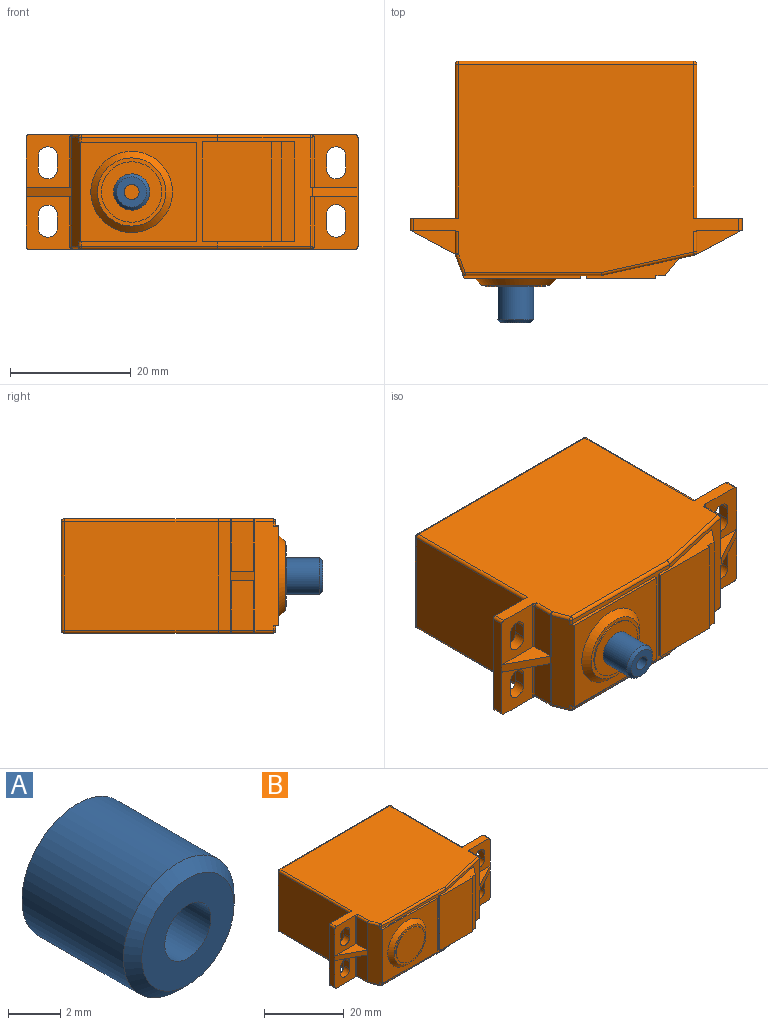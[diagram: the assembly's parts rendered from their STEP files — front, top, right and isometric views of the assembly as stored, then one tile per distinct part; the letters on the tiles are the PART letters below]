
ASSEMBLY  parts=2 mates=1
PART A: 5 faces, bbox 6x6x6 mm
  f0: cylinder r=3mm len=6mm, axis (0,1,0), area 103.7mm2, adj f2,f4
  f1: plane 5x5mm, normal (0,-1,0), area 14.7mm2, adj f3,f4
  f2: plane 6x6mm, normal (0,1,0), area 23.4mm2, adj f0,f3
  f3: cylinder r=1.25mm len=6mm, axis (0,-1,0), area 47.1mm2, adj f1,f2
  f4: cone r=2.5mm half-angle=45deg, axis (0,1,0), area 12.2mm2, adj f0,f1
PART B: 103 faces, bbox 55x37.3x19.5 mm
  f0: plane 19x8mm, normal (0,1,0), area 112.7mm2, adj f7,f11,f13,f31,f41,f42,f43,f44
  f1: plane 8.75x7.44mm, normal (0,-1,0), area 48.7mm2, adj f13,f31,f38,f45,f46,f47,f48,f59
  f2: plane 8.25x3.35mm, normal (1,0,0), area 27.6mm2, adj f38,f72,f73,f97
  f3: plane 8.75x7.44mm, normal (0,-1,0), area 48.3mm2, adj f11,f31,f39,f41,f42,f43,f44,f60
  f4: plane 8.25x3.66mm, normal (-1,0,0), area 30.2mm2, adj f35,f79,f82,f99
  f5: plane 8.75x7.44mm, normal (0,-1,0), area 48.7mm2, adj f11,f30,f36,f53,f54,f55,f56,f57
  f6: cone r=5.45mm half-angle=45deg, axis (0,1,0), area 60.6mm2, adj f15,f34
  f7: plane 25.5x18mm, normal (1,0,0), area 459mm2, adj f0,f85,f91,f94
  f8: plane 25.5x18mm, normal (-1,0,0), area 459mm2, adj f28,f83,f87,f88
  f9: plane 15.29x3.34mm, normal (0,0,1), area 20.7mm2, adj f10,f18,f22,f23,f25,f26,f27
  f10: plane 16.5x11.5mm, normal (0,-1,0), area 189.7mm2, adj f9,f23,f24,f25
  f11: plane 54x34.5mm, normal (0,0,-1), area 1347.9mm2, adj f0,f3,f5,f28,f57,f60,f61,f64
  f12: plane 8.25x3.35mm, normal (1,0,0), area 27.6mm2, adj f39,f68,f71,f95
  f13: plane 54x34.5mm, normal (0,0,1), area 1347.9mm2, adj f0,f1,f28,f29,f58,f59,f72,f75
  f14: plane 8.25x3.66mm, normal (-1,0,0), area 30.2mm2, adj f36,f61,f62,f101
  f15: plane 19.25x16.5mm, normal (0,-1,0), area 174.5mm2, adj f6,f17,f19,f20,f21
  f16: plane 39x18mm, normal (0,1,0), area 702mm2, adj f86,f87,f91,f92
  f17: plane 18x4mm, normal (-0.94,-0.35,0), area 74.1mm2, adj f15,f20,f21,f35,f36,f37,f62,f64
  f18: plane 18x15.75mm, normal (0.22,-0.98,0), area 67.5mm2, adj f9,f22,f24,f27,f38,f39,f40,f69
  f19: plane 16.5x0.5mm, normal (1,0,0), area 8.3mm2, adj f15,f20,f21,f22
  f20: plane 19.56x0.82mm, normal (0,0,-1), area 9.7mm2, adj f15,f17,f19,f22,f65
  f21: plane 19.56x0.82mm, normal (0,0,1), area 9.7mm2, adj f15,f17,f19,f22,f77
  f22: plane 22.59x18mm, normal (0,-1,0), area 50.4mm2, adj f9,f18,f19,f20,f21,f23,f24,f65
  f23: plane 16.5x0.5mm, normal (-1,0,0), area 8.3mm2, adj f9,f10,f22,f24
  f24: plane 15.29x3.34mm, normal (0,0,-1), area 20.7mm2, adj f10,f18,f22,f23,f25,f26,f27
  f25: plane 16.5x0.5mm, normal (1,0,0), area 8.3mm2, adj f9,f10,f24,f26
  f26: plane 16.5x1.51mm, normal (0,-1,0), area 25mm2, adj f9,f24,f25,f27
  f27: plane 16.5x2.84mm, normal (0.78,-0.63,0), area 60.1mm2, adj f9,f18,f24,f26
  f28: plane 19x8mm, normal (0,1,0), area 113mm2, adj f8,f11,f13,f30,f49,f50,f51,f52
  f29: plane 8.75x7.44mm, normal (0,-1,0), area 48.7mm2, adj f13,f30,f35,f49,f50,f51,f52,f58
  f30: plane 18x2mm, normal (-1,0,0), area 36mm2, adj f5,f28,f29,f37,f57,f58
  f31: plane 18x2mm, normal (1,0,0), area 36mm2, adj f0,f1,f3,f40,f59,f60
  f32: plane 10x10mm, normal (0,-1,0), area 78.5mm2, adj f33
  f33: cylinder r=5mm len=10mm, axis (0,-1,0), area 6.3mm2, adj f32,f34
  f34: plane 11.3x11.3mm, normal (0,-1,0), area 21.7mm2, adj f6,f33
  f35: plane 7.53x4.09mm, normal (0,0,1), area 15mm2, adj f4,f17,f29,f37,f82,f99
  f36: plane 7.53x4.09mm, normal (0,0,-1), area 15mm2, adj f5,f14,f17,f37,f62,f101
  f37: plane 7.5x4mm, normal (-0.47,-0.88,0), area 12.8mm2, adj f17,f30,f35,f36
  f38: plane 7.89x4.09mm, normal (0,0,1), area 15mm2, adj f1,f2,f18,f40,f73,f97
  f39: plane 7.89x4.09mm, normal (0,0,-1), area 15mm2, adj f3,f12,f18,f40,f71,f95
  f40: plane 7.5x4mm, normal (0.47,-0.88,0), area 12.8mm2, adj f18,f31,f38,f39
  f41: cylinder r=1.6mm len=3.2mm, axis (0,-1,0), area 10.1mm2, adj f0,f3,f42,f44
  f42: plane 2.2x2mm, normal (-1,0,0), area 4.4mm2, adj f0,f3,f41,f43
  f43: cylinder r=1.6mm len=3.2mm, axis (0,-1,0), area 10.1mm2, adj f0,f3,f42,f44
  f44: plane 2.2x2mm, normal (1,0,0), area 4.4mm2, adj f0,f3,f41,f43
  f45: plane 2.1x2mm, normal (-1,0,0), area 4.2mm2, adj f0,f1,f46,f48
  f46: cylinder r=1.6mm len=3.2mm, axis (0,-1,0), area 10.1mm2, adj f0,f1,f45,f47
  f47: plane 2.1x2mm, normal (1,0,0), area 4.2mm2, adj f0,f1,f46,f48
  f48: cylinder r=1.6mm len=3.2mm, axis (0,-1,0), area 10.1mm2, adj f0,f1,f45,f47
  f49: cylinder r=1.6mm len=3.2mm, axis (0,-1,0), area 10.1mm2, adj f28,f29,f50,f52
  f50: plane 2.1x2mm, normal (1,0,0), area 4.2mm2, adj f28,f29,f49,f51
  f51: cylinder r=1.6mm len=3.2mm, axis (0,-1,0), area 10.1mm2, adj f28,f29,f50,f52
  f52: plane 2.1x2mm, normal (-1,0,0), area 4.2mm2, adj f28,f29,f49,f51
  f53: cylinder r=1.6mm len=3.2mm, axis (0,-1,0), area 10.1mm2, adj f5,f28,f54,f56
  f54: plane 2.1x2mm, normal (-1,0,0), area 4.2mm2, adj f5,f28,f53,f55
  f55: cylinder r=1.6mm len=3.2mm, axis (0,-1,0), area 10.1mm2, adj f5,f28,f54,f56
  f56: plane 2.1x2mm, normal (1,0,0), area 4.2mm2, adj f5,f28,f53,f55
  f57: cylinder r=0.5mm len=2mm, axis (0,1,0), area 1.6mm2, adj f5,f11,f28,f30
  f58: cylinder r=0.5mm len=2mm, axis (0,-1,0), area 1.6mm2, adj f13,f28,f29,f30
  f59: cylinder r=0.5mm len=2mm, axis (0,-1,0), area 1.6mm2, adj f0,f1,f13,f31
  f60: cylinder r=0.5mm len=2mm, axis (0,1,0), area 1.6mm2, adj f0,f3,f11,f31
  f61: cylinder r=0.5mm len=3.66mm, axis (0,-1,0), area 2.9mm2, adj f11,f14,f63,f102
  f62: cylinder r=0.5mm len=8.25mm, axis (0,0,-1), area 1.5mm2, adj f14,f17,f36,f63
  f63: sphere r=0.5mm, area 0.1mm2, adj f61,f62,f64
  f64: cylinder r=0.5mm len=3.27mm, axis (-0.35,0.94,0), area 2.6mm2, adj f11,f17,f63,f66
  f65: cylinder r=0.5mm len=0.75mm, axis (0,0,1), area 0.5mm2, adj f17,f20,f22,f66
  f66: sphere r=0.5mm, area 0.3mm2, adj f64,f65,f67
  f67: cylinder r=0.5mm len=22.59mm, axis (-1,0,0), area 17.7mm2, adj f11,f22,f66,f69
  f68: cylinder r=0.5mm len=3.35mm, axis (0,1,0), area 2.6mm2, adj f11,f12,f70,f96
  f69: cylinder r=0.5mm len=15.47mm, axis (0.98,0.22,0), area 12.3mm2, adj f11,f18,f67,f70
  f70: sphere r=0.5mm, area 0.3mm2, adj f68,f69,f71
  f71: cylinder r=0.5mm len=8.25mm, axis (0,0,1), area 5.6mm2, adj f12,f18,f39,f70
  f72: cylinder r=0.5mm len=3.35mm, axis (0,-1,0), area 2.6mm2, adj f2,f13,f74,f98
  f73: cylinder r=0.5mm len=8.25mm, axis (0,0,1), area 5.6mm2, adj f2,f18,f38,f74
  f74: sphere r=0.5mm, area 0.3mm2, adj f72,f73,f75
  f75: cylinder r=0.5mm len=15.47mm, axis (0.98,0.22,0), area 12.3mm2, adj f13,f18,f74,f76
  f76: cylinder r=0.5mm len=22.59mm, axis (1,0,0), area 17.7mm2, adj f13,f22,f75,f78
  f77: cylinder r=0.5mm len=0.75mm, axis (0,0,-1), area 0.5mm2, adj f17,f21,f22,f78
  f78: sphere r=0.5mm, area 0.3mm2, adj f76,f77,f80
  f79: cylinder r=0.5mm len=3.66mm, axis (0,1,0), area 2.9mm2, adj f4,f13,f81,f100
  f80: cylinder r=0.5mm len=3.27mm, axis (-0.35,0.94,0), area 2.6mm2, adj f13,f17,f78,f81
  f81: sphere r=0.5mm, area 0.1mm2, adj f79,f80,f82
  f82: cylinder r=0.5mm len=8.25mm, axis (0,0,-1), area 1.5mm2, adj f4,f17,f35,f81
  f83: cylinder r=0.5mm len=25.5mm, axis (0,1,0), area 20mm2, adj f8,f13,f28,f84
  f84: sphere r=0.5mm, area 0.4mm2, adj f83,f86,f87
  f85: cylinder r=0.5mm len=25.5mm, axis (0,-1,0), area 20mm2, adj f0,f7,f13,f89
  f86: cylinder r=0.5mm len=39mm, axis (-1,0,0), area 30.6mm2, adj f13,f16,f84,f89
  f87: cylinder r=0.5mm len=18mm, axis (0,0,-1), area 14.1mm2, adj f8,f16,f84,f90
  f88: cylinder r=0.5mm len=25.5mm, axis (0,-1,0), area 20mm2, adj f8,f11,f28,f90
  f89: sphere r=0.5mm, area 0.4mm2, adj f85,f86,f91
  f90: sphere r=0.5mm, area 0.4mm2, adj f87,f88,f92
  f91: cylinder r=0.5mm len=18mm, axis (0,0,1), area 14.1mm2, adj f7,f16,f89,f93
  f92: cylinder r=0.5mm len=39mm, axis (1,0,0), area 30.6mm2, adj f11,f16,f90,f93
  f93: sphere r=0.5mm, area 0.4mm2, adj f91,f92,f94
  f94: cylinder r=0.5mm len=25.5mm, axis (0,1,0), area 20mm2, adj f0,f7,f11,f93
  f95: plane 8.25x0.25mm, normal (0.71,-0.71,0), area 2.9mm2, adj f3,f12,f39,f96
  f96: cone r=0.75mm half-angle=45deg, axis (0,1,0), area 0.2mm2, adj f3,f11,f68,f95
  f97: plane 8.25x0.25mm, normal (0.71,-0.71,0), area 2.9mm2, adj f1,f2,f38,f98
  f98: cone r=0.75mm half-angle=45deg, axis (0,1,0), area 0.2mm2, adj f1,f13,f72,f97
  f99: plane 8.25x0.25mm, normal (-0.71,-0.71,0), area 2.9mm2, adj f4,f29,f35,f100
  f100: cone r=0.75mm half-angle=45deg, axis (0,1,0), area 0.2mm2, adj f13,f29,f79,f99
  f101: plane 8.25x0.25mm, normal (-0.71,-0.71,0), area 2.9mm2, adj f5,f14,f36,f102
  f102: cone r=0.75mm half-angle=45deg, axis (0,1,0), area 0.2mm2, adj f5,f11,f61,f101
PLACE A t=(-16.12,3.76,-13.7)mm
PLACE B t=(-16.12,3.76,-13.7)mm
MATE revolute B.f6 <-> A.f0  axis (0,-1,0) through (-26.12,-33.54,-13.7)mm
